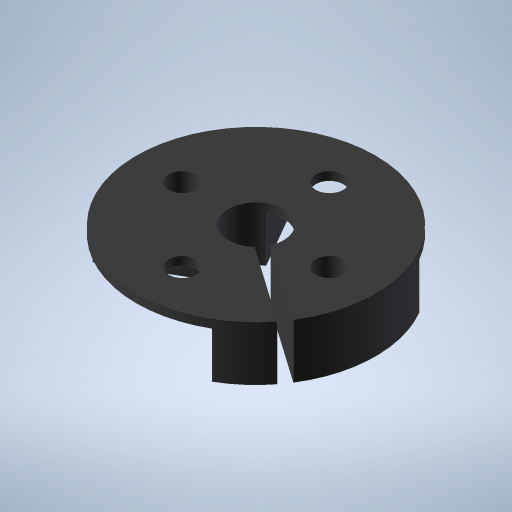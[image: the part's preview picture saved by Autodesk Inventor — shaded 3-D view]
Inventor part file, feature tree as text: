
AUTODESK INVENTOR PART (.ipt)
format: ipt  version: 2024 (Build 280153000, 153)  size: 296,960 bytes
history: native  units: in
note: dims shown in document units (in); Inventor stores cm internally (conversion verified against a paired STEP export)
features: other x4, extrude x4, hole x4, sketch x1
ambient origin geometry x8: Origin, YZ Plane, XZ Plane, XY Plane, X Axis, Y Axis, Z Axis, Center Point
bodies: Solid1 (feature_tree)
feature tree (13):
  other  "Annotations"
  sketch  "Sketch1"  dims[d0=0.3in d1=1.3in d2=0.4in d3=0.4in d4=0.12in d5=0.12in d6=0.296in d7=0.0in d8=0.396in d9=1.204in d10=0.4in d11=0.1875in d12=60.0deg d13=0.25in d14=0.0in d15=0.25in d16=0.0in d17=0.032in d18=0.032in d19=0.07in d24=0.12in d25=0.4in d26=0.12in d41=0.0625in d42=0.9963in d43=0.032in d44=0.032in d45=0.296in d46=0.0in d53=0.15in d54=0.5in d55=0.279in d56=0.25in d57=0.5635in d58=0.5in d59=0.0in d60=0.15in d61=0.75in d62=0.375in d63=0.25in d64=0.5635in d65=1.0in d66=0.0in d67=0.15in d68=0.75in d69=0.375in d70=0.25in d71=0.5635in d72=1.0in d73=0.0in d74=0.15in d75=0.75in d76=0.375in d77=0.25in d78=0.5635in d79=1.0in d80=0.0in d47=0.046in d48=2.2514in d49=0.65in d50=0.0in d51=0.3937in d52=0.296in]
  extrude  "Extrusion1"  Depth=0.296in
  extrude  "Extrusion2"  Depth=0.296in
  extrude  "Extrusion3"  Depth=0.296in
  extrude  "Extrusion6"  Depth=0.296in
  hole  "Hole3"  [1 undecoded]
  hole  "Hole4"  [1 undecoded]
  hole  "Hole5"  [1 undecoded]
  hole  "Hole6"  [1 undecoded]
  other  "Linear Dimension 1"
  other  "Radial Dimension 1"
  other  "Linear Dimension 2"
note: 4 required parameter values undecoded (feature->parameter linkage not recoverable at this tier; creation-order binding heuristic only, values carry confidence <= 0.55)
